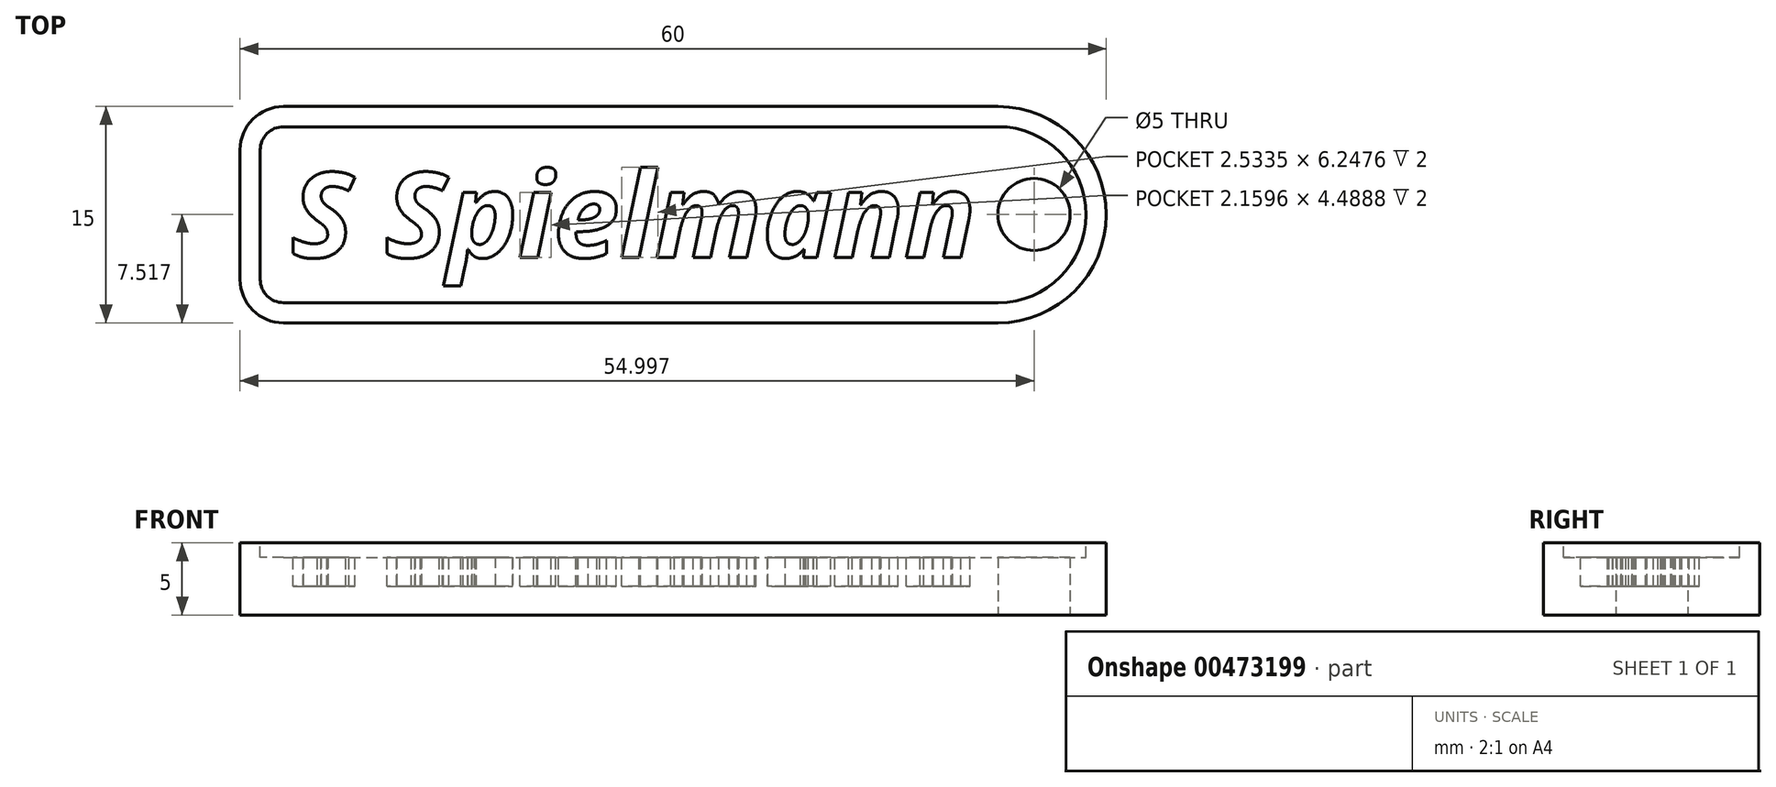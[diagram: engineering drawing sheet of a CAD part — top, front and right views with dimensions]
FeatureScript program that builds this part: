
annotation { "Feature Type Name" : "Feature", "Feature Type Description" : "" }
export const myFeature = defineFeature(function(context is Context, id is Id, definition is map)
    precondition{}
    {
        {
            var Q0;
            Q0=qCreatedBy(makeId("Top.planeOp"),FACE);
            var sketch = newSketch(context, id + "F0", { "sketchPlane" : qUnion([Q0])});
            skLineSegment(sketch, "E0.bottom", {"start": v(-20.01, 7.5) * mm, "end": v(29.49, 7.5) * mm});
            skLineSegment(sketch, "E0.top", {"start": v(-20.01, -7.5) * mm, "end": v(29.49, -7.5) * mm});
            skLineSegment(sketch, "E0.left", {"start": v(-23.01, 4.5) * mm, "end": v(-23.01, -4.5) * mm});
            skArc(sketch, "E1", {"start": v(29.49, -7.5) * mm, "mid": v(36.99, 0) * mm, "end": v(29.49, 7.5) * mm});
            skPoint(sketch, "E2.visualSharp", {"position": v(-23.01, 7.5) * mm});
            skArc(sketch, "E2.filletArc", {"start": v(-20.01, 7.5) * mm, "mid": v(-22.13, 6.62) * mm, "end": v(-23.01, 4.5) * mm});
            skPoint(sketch, "E3.visualSharp", {"position": v(-23.01, -7.5) * mm});
            skArc(sketch, "E3.filletArc", {"start": v(-23.01, -4.5) * mm, "mid": v(-22.13, -6.62) * mm, "end": v(-20.01, -7.5) * mm});
            skCircle(sketch, "E4", {"center": v(31.99, 0.02) * mm, "radius": 2.5 * mm});
            skSolve(sketch);
        }
        {
            var Q0;
            Q0 = qSketchRegion(id + "F0", true);
            extrude(context, id + "F1", {"entities" : qUnion([Q0]), "depth" : 5 * mm});
        }
        {
            var Q0;
            Q0=makeQuery(id+"F1.opExtrude","CAP_FACE",FACE,{"disambiguationData":[OSD([sQuery(id+"F0.wireOp",EDGE,"E0.bottom"),sQuery(id+"F0.wireOp",EDGE,"E0.top"),sQuery(id+"F0.wireOp",EDGE,"E0.left"),sQuery(id+"F0.wireOp",EDGE,"E1"),sQuery(id+"F0.wireOp",EDGE,"E2.filletArc"),sQuery(id+"F0.wireOp",EDGE,"E3.filletArc"),sQuery(id+"F0.wireOp",EDGE,"E4")])],"isStart":false});
            var sketch = newSketch(context, id + "F2", { "sketchPlane" : qUnion([Q0])});
            skText(sketch, "E5", { "text": "S Spielmann", "fontName": "OpenSans-BoldItalic.ttf"});
            const initialGuessF2  = {"E5": [-0.0195, -0.00296, 1, 0, 0.00592]};
            skSetInitialGuess(sketch, initialGuessF2);
            skSolve(sketch);
        }
        {
            var Q0;
            Q0 = qSketchRegion(id + "F2", true);
            extrude(context, id + "F3", {"entities" : qUnion([Q0]), "operationType" : NewBodyOperationType.REMOVE, "oppositeDirection" : true, "depth" : 3 * mm});
        }
        {
            var Q0;
            {var subQ0=sQuery(id+"F0.wireOp",EDGE,"E0.top");var subQ1=sQuery(id+"F0.wireOp",EDGE,"E1");var subQ2=sQuery(id+"F0.wireOp",EDGE,"E0.bottom");var subQ3=sQuery(id+"F0.wireOp",EDGE,"E2.filletArc");var subQ4=sQuery(id+"F0.wireOp",EDGE,"E3.filletArc");var subQ5=sQuery(id+"F0.wireOp",EDGE,"E4");var subQ6=sQuery(id+"F0.wireOp",EDGE,"E0.left");Q0=makeQuery(id+"F3.boolean.opBoolean","SPLIT",FACE,{"disambiguationData":[TD([makeQuery(id+"F1.opExtrude","SWEPT_FACE",FACE,{"disambiguationData":[OSD([subQ2])]})])],"derivedFrom":makeQuery(id+"F1.opExtrude","CAP_FACE",FACE,{"disambiguationData":[OSD([subQ2,subQ0,subQ6,subQ1,subQ3,subQ4,subQ5])],"isStart":false})});}
            var sketch = newSketch(context, id + "F4", { "sketchPlane" : qUnion([Q0])});
            skArc(sketch, "E6.0", {"start": v(-20.01, 6.1) * mm, "mid": v(-21.14, 5.63) * mm, "end": v(-21.61, 4.5) * mm});
            skArc(sketch, "E6.1", {"start": v(29.49, -6.1) * mm, "mid": v(35.59, 0) * mm, "end": v(29.49, 6.1) * mm});
            skLineSegment(sketch, "E6.2", {"start": v(-20.01, -6.1) * mm, "end": v(29.49, -6.1) * mm});
            skLineSegment(sketch, "E6.3", {"start": v(-20.01, 6.1) * mm, "end": v(29.49, 6.1) * mm});
            skArc(sketch, "E6.4", {"start": v(-21.61, -4.5) * mm, "mid": v(-21.14, -5.63) * mm, "end": v(-20.01, -6.1) * mm});
            skLineSegment(sketch, "E6.5", {"start": v(-21.61, 4.5) * mm, "end": v(-21.61, -4.5) * mm});
            skSolve(sketch);
        }
        {
            var Q0;
            Q0 = qSketchRegion(id + "F4", true);
            extrude(context, id + "F5", {"entities" : qUnion([Q0]), "operationType" : NewBodyOperationType.REMOVE, "oppositeDirection" : true, "depth" : 1 * mm});
        }
    });
